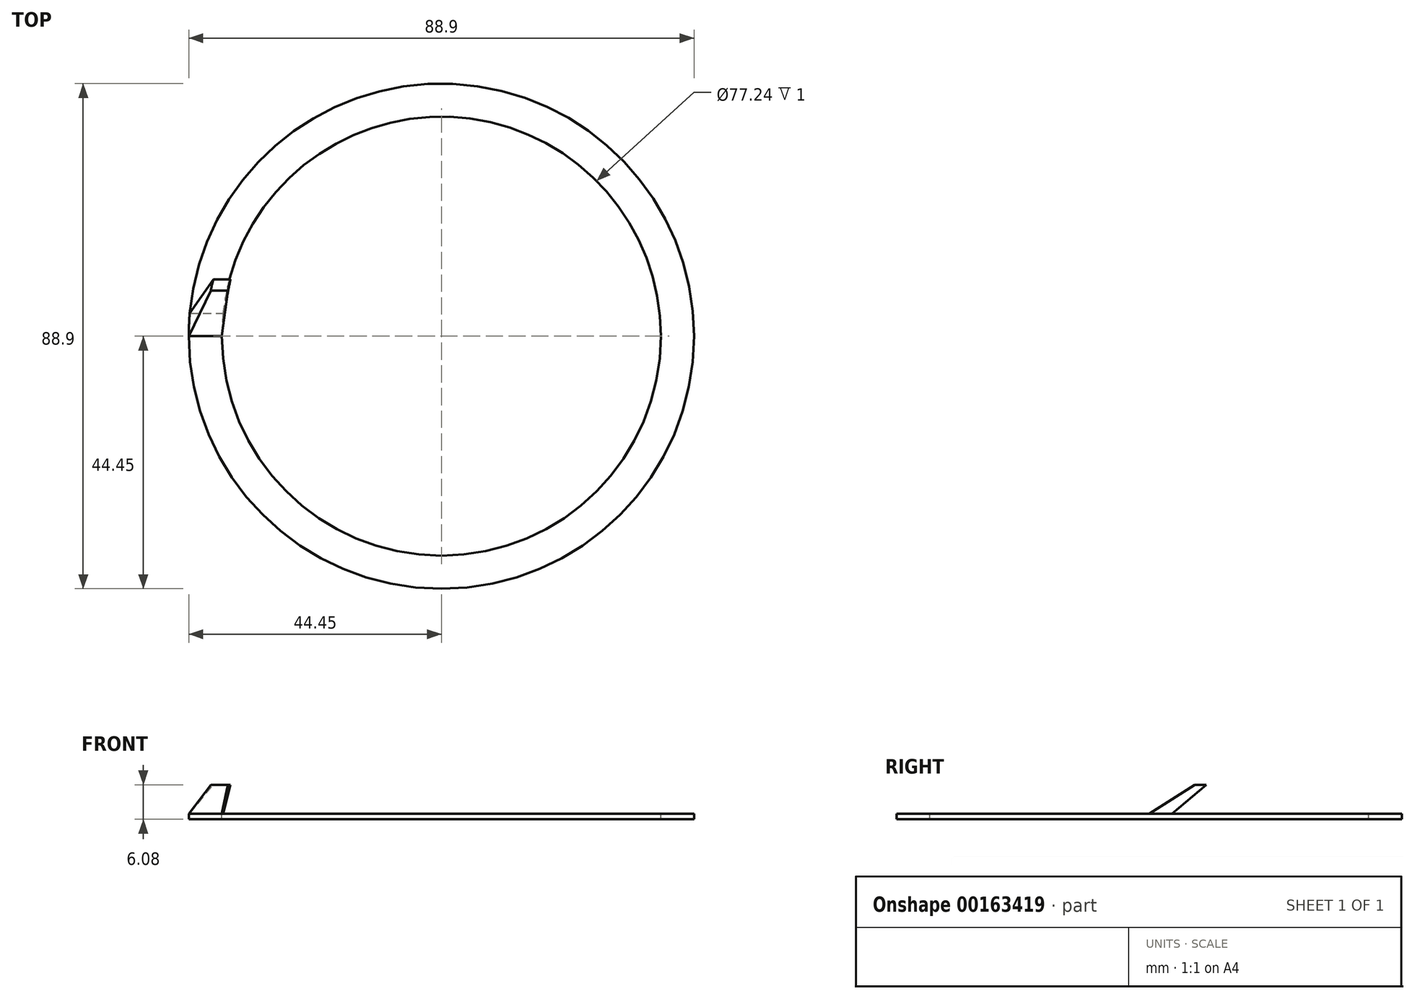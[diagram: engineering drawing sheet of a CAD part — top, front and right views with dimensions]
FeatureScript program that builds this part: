
annotation { "Feature Type Name" : "Feature", "Feature Type Description" : "" }
export const myFeature = defineFeature(function(context is Context, id is Id, definition is map)
    precondition{}
    {
        {
            var Q0;
            Q0=qCreatedBy(makeId("Top.planeOp"),FACE);
            cPlane(context, id + "F0", {"entities" : qUnion([Q0]), "cplaneType" : CPlaneType.OFFSET, "offset" : 5.08 * mm, "width" : 152.4 * mm, "height" : 152.4 * mm});
        }
        {
            var Q0;
            Q0=qCreatedBy(makeId("Top.planeOp"),FACE);
            var sketch = newSketch(context, id + "F1", { "sketchPlane" : qUnion([Q0]), "disableImprinting" : false});
            skCircle(sketch, "E0", {"center": v(0, 0) * mm, "radius": 44.45 * mm});
            skLineSegment(sketch, "E1.bottom", {"start": v(-44.45, 0) * mm, "end": v(-38.62, 0) * mm});
            skLineSegment(sketch, "E1.top", {"start": v(-44.27, 4) * mm, "end": v(-38.41, 4) * mm});
            skCircle(sketch, "E2", {"center": v(0, 0) * mm, "radius": 38.62 * mm});
            skSolve(sketch);
        }
        {
            var Q0;
            Q0=qCreatedBy(id+"F0.planeOp",FACE);
            var sketch = newSketch(context, id + "F2", { "sketchPlane" : qUnion([Q0]), "disableImprinting" : false});
            skLineSegment(sketch, "E3.bottom", {"start": v(-37.1, 10) * mm, "end": v(-40.13, 10) * mm});
            skLineSegment(sketch, "E3.top", {"start": v(-37.58, 8) * mm, "end": v(-40.58, 8) * mm});
            skCircle(sketch, "E4", {"center": v(0, 0) * mm, "radius": 49.53 * mm, "construction": true});
            skCircle(sketch, "E5", {"center": v(0, 0) * mm, "radius": 38.42 * mm});
            skCircle(sketch, "E6", {"center": v(0, 0) * mm, "radius": 41.36 * mm});
            skLineSegment(sketch, "E7", {"start": v(0, 0) * mm, "end": v(-49.53, 0) * mm, "construction": true});
            skSolve(sketch);
        }
        {
            var Q0;
            {var subQ0=sQuery(id+"F1.wireOp",EDGE,"E1.bottom");Q0=makeQuery(id+"F1.imprint","IMPRINT",FACE,{"disambiguationData":[TD([[makeQuery(id+"F1.imprint","IMPRINT",EDGE,{"derivedFrom":subQ0}),-1.0]])]});}
            var Q1;
            {var subQ0=sQuery(id+"F1.wireOp",EDGE,"E1.bottom");Q1=makeQuery(id+"F1.imprint","IMPRINT",FACE,{"disambiguationData":[TD([[makeQuery(id+"F1.imprint","IMPRINT",EDGE,{"derivedFrom":subQ0}),1.0]])]});}
            extrude(context, id + "F3", {"entities" : qUnion([Q0, Q1]), "oppositeDirection" : true, "depth" : 1 * mm});
        }
        {
            var Q0;
            Q0=makeQuery(id+"F1.imprint","IMPRINT",FACE,{"disambiguationData":[TD([[makeQuery(id+"F1.imprint","IMPRINT",EDGE,{"derivedFrom":sQuery(id+"F1.wireOp",EDGE,"E1.bottom")}),1.0]])]});
            var Q1;
            Q1=makeQuery(id+"F2.imprint","IMPRINT",FACE,{"disambiguationData":[TD([[makeQuery(id+"F2.imprint","IMPRINT",EDGE,{"derivedFrom":sQuery(id+"F2.wireOp",EDGE,"E3.bottom")}),1.0]])]});
            loft(context, id + "F4", {"operationType" : NewBodyOperationType.ADD, "sheetProfilesArray" : [{ "sheetProfileEntities" : qUnion([Q0]) }, { "sheetProfileEntities" : qUnion([Q1]) }]});
        }
        {
            var Q0;
            Q0=qCreatedBy(makeId("Front.planeOp"),FACE);
            var sketch = newSketch(context, id + "F5", { "sketchPlane" : qUnion([Q0])});
            skLineSegment(sketch, "E8", {"start": v(0, 0) * mm, "end": v(0, 19.82) * mm, "construction": true});
            skSolve(sketch);
        }
    });
